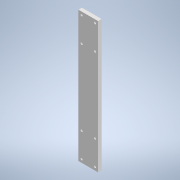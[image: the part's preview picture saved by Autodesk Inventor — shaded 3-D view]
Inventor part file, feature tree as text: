
AUTODESK INVENTOR PART (.ipt)
format: ipt  version: 2021 (Build 250183000, 183)  size: 125,440 bytes
history: native  units: mm
features: reference x3, other x3, extrude x2, sketch x2, projected_geometry x1
ambient origin geometry x8: Origin, YZ Plane, XZ Plane, XY Plane, X Axis, Y Axis, Z Axis, Center Point
bodies: Solid1 (feature_tree)
feature tree (11):
  extrude  "Extrusion1"  Depth=5.0mm
  extrude  "Extrusion2"  Depth=10.0mm
  sketch  "Sketch1"  dims[d0=5.0mm d1=0.0mm d2=4.5mm]
  reference  "Reference1"
  reference  "Reference2"
  sketch  "Sketch2"  dims[d3=4.5mm d4=3.0mm d5=44.0mm d6=28.000001mm d7=20.0mm d9=19.0mm d10=20.0mm d12=35.0mm d15=186.0mm d16=20.0mm d18=142.0mm d19=10.0mm d21=10.0mm d23=0.0mm d24=0.0mm]
  projected_geometry  "Projected Loop1"
  reference  "Reference3"
  other  "4_WheelsSwerve01.iam"
  other  "Part10"
  other  "Part10:2"
